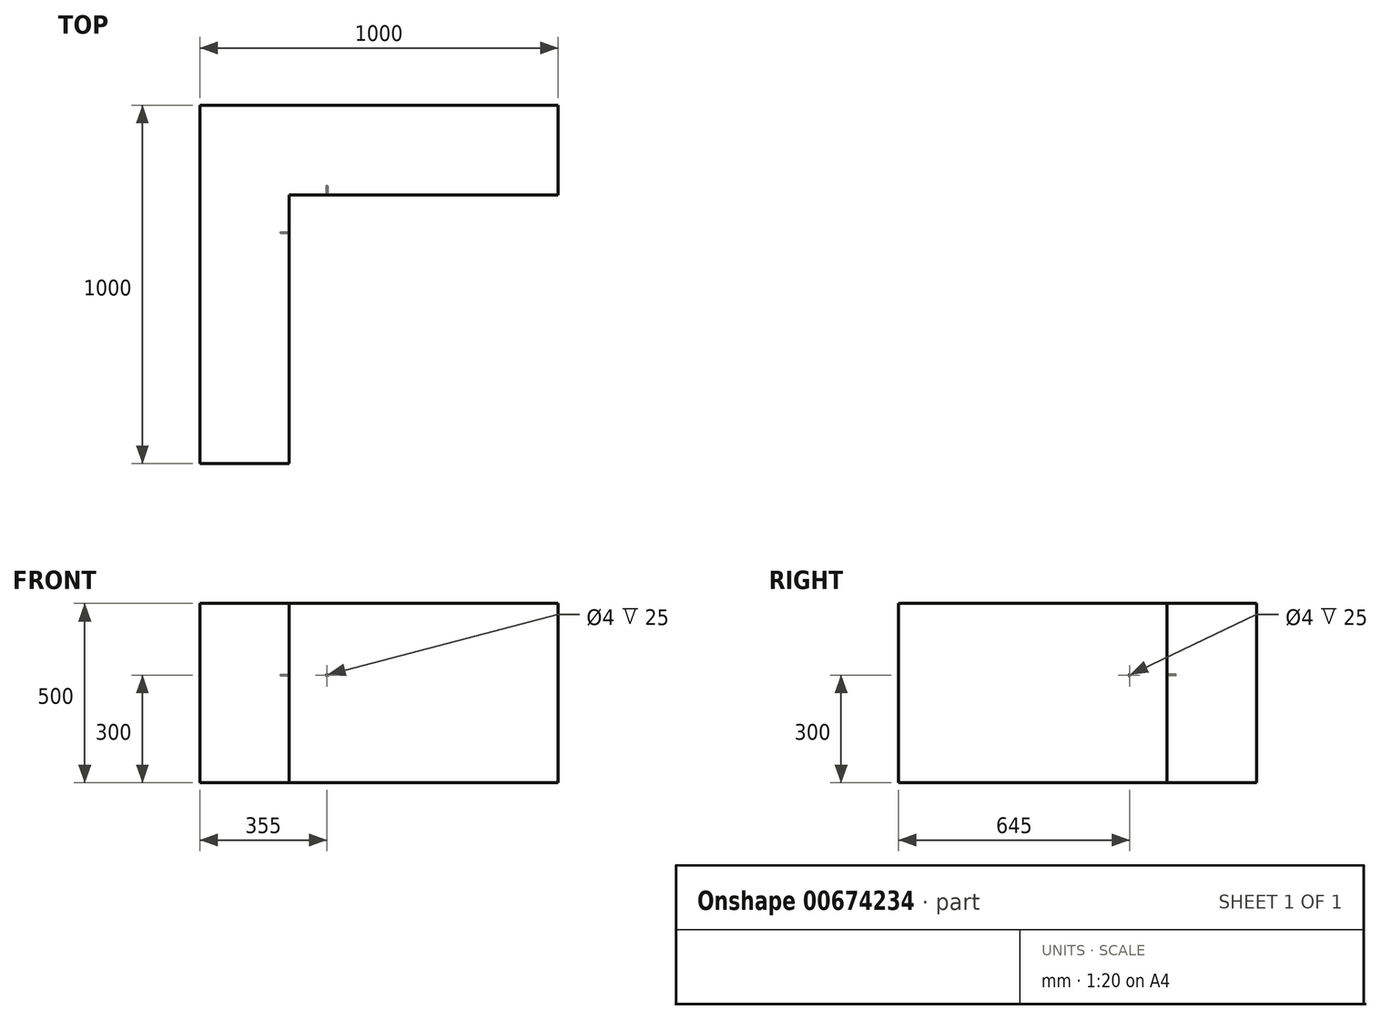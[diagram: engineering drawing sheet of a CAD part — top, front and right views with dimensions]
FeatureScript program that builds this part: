
annotation { "Feature Type Name" : "Feature", "Feature Type Description" : "" }
export const myFeature = defineFeature(function(context is Context, id is Id, definition is map)
    precondition{}
    {
        {
            var Q0;
            Q0=qCreatedBy(makeId("Top.planeOp"),FACE);
            var sketch = newSketch(context, id + "F0", { "sketchPlane" : qUnion([Q0])});
            skLineSegment(sketch, "E0.bottom", {"start": v(0, 0) * mm, "end": v(-250, 0) * mm});
            skLineSegment(sketch, "E0.top", {"start": v(0, -750) * mm, "end": v(-250, -750) * mm});
            skLineSegment(sketch, "E0.left", {"start": v(0, 0) * mm, "end": v(0, -750) * mm});
            skLineSegment(sketch, "E0.right", {"start": v(-250, 0) * mm, "end": v(-250, -750) * mm});
            skLineSegment(sketch, "E1.bottom", {"start": v(-250, 0) * mm, "end": v(750, 0) * mm});
            skLineSegment(sketch, "E1.top", {"start": v(-250, 250) * mm, "end": v(750, 250) * mm});
            skLineSegment(sketch, "E1.left", {"start": v(-250, 0) * mm, "end": v(-250, 250) * mm});
            skLineSegment(sketch, "E1.right", {"start": v(750, 0) * mm, "end": v(750, 250) * mm});
            skSolve(sketch);
        }
        {
            var Q0;
            {var subQ0=makeQuery(id+"F0.imprint","IMPRINT",EDGE,{"derivedFrom":sQuery(id+"F0.wireOp",EDGE,"E0.bottom")});Q0=qUnion([makeQuery(id+"F0.imprint","IMPRINT",FACE,{"disambiguationData":[TD([[subQ0,1.0]])]}),makeQuery(id+"F0.imprint","IMPRINT",FACE,{"disambiguationData":[TD([[subQ0,-1.0]])]})]);}
            extrude(context, id + "F1", {"entities" : qUnion([Q0]), "depth" : 500 * mm, "offsetDistance" : 25 * mm});
        }
        {
            var Q0;
            Q0=makeQuery(id+"F1.opExtrude","SWEPT_FACE",FACE,{"disambiguationData":[OSD([sQuery(id+"F0.wireOp",EDGE,"E0.left")])]});
            var sketch = newSketch(context, id + "F2", { "sketchPlane" : qUnion([Q0])});
            skCircle(sketch, "E2", {"center": v(-105, 300) * mm, "radius": 2 * mm});
            skSolve(sketch);
        }
        {
            var Q0;
            Q0 = qSketchRegion(id + "F2", true);
            extrude(context, id + "F3", {"entities" : qUnion([Q0]), "operationType" : NewBodyOperationType.REMOVE, "oppositeDirection" : true, "depth" : 25 * mm, "offsetDistance" : 25 * mm});
        }
        {
            var Q0;
            Q0=makeQuery(id+"F1.opExtrude","SWEPT_FACE",FACE,{"disambiguationData":[OSD([sQuery(id+"F0.wireOp",EDGE,"E1.bottom")])]});
            var sketch = newSketch(context, id + "F4", { "sketchPlane" : qUnion([Q0])});
            skCircle(sketch, "E3", {"center": v(105, 300) * mm, "radius": 2 * mm});
            skSolve(sketch);
        }
        {
            var Q0;
            Q0 = qSketchRegion(id + "F4", true);
            extrude(context, id + "F5", {"entities" : qUnion([Q0]), "operationType" : NewBodyOperationType.REMOVE, "oppositeDirection" : true, "depth" : 25 * mm, "offsetDistance" : 25 * mm});
        }
    });
